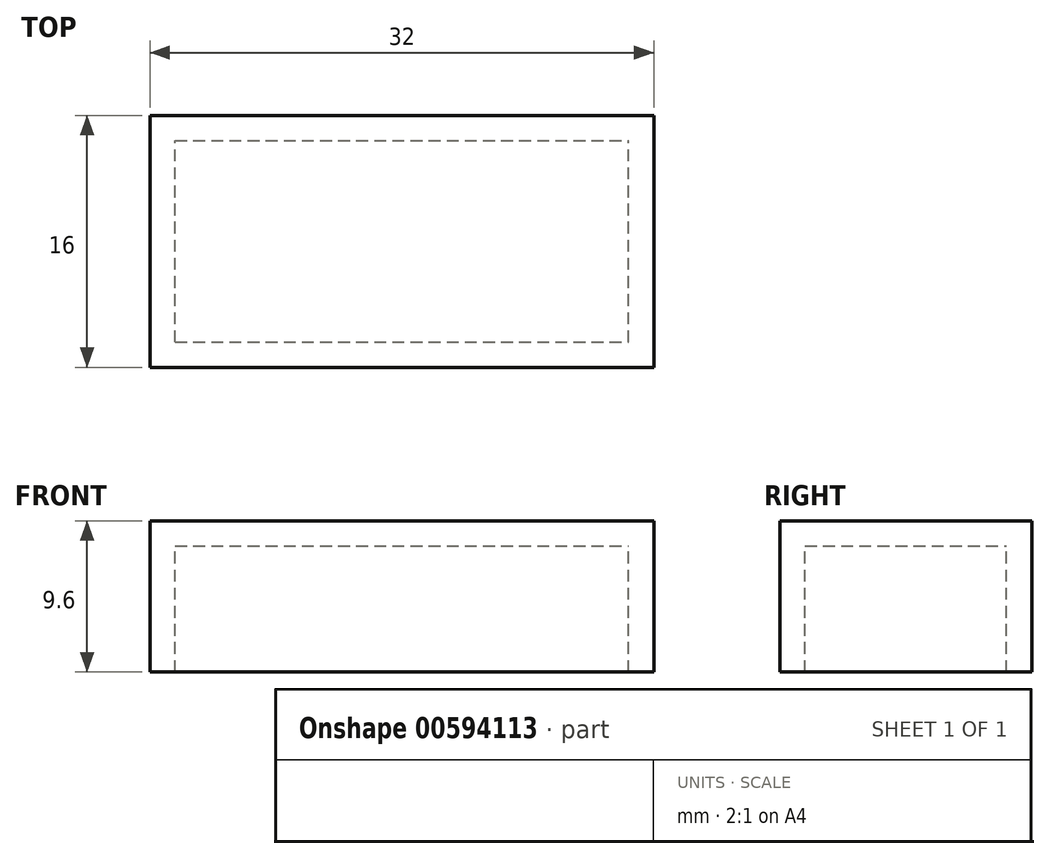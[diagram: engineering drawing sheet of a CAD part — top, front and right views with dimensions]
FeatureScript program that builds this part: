
annotation { "Feature Type Name" : "Feature", "Feature Type Description" : "" }
export const myFeature = defineFeature(function(context is Context, id is Id, definition is map)
    precondition{}
    {
        {
            var Q0;
            Q0=qCreatedBy(makeId("Front.planeOp"),FACE);
            var sketch = newSketch(context, id + "F0", { "sketchPlane" : qUnion([Q0])});
            skLineSegment(sketch, "E0.bottom", {"start": v(-32.95, -27.77) * mm, "end": v(-0.95, -27.77) * mm});
            skLineSegment(sketch, "E0.top", {"start": v(-32.95, -18.17) * mm, "end": v(-0.95, -18.17) * mm});
            skLineSegment(sketch, "E0.left", {"start": v(-32.95, -27.77) * mm, "end": v(-32.95, -18.17) * mm});
            skLineSegment(sketch, "E0.right", {"start": v(-0.95, -27.77) * mm, "end": v(-0.95, -18.17) * mm});
            skSolve(sketch);
        }
        {
            var Q0;
            Q0 = qSketchRegion(id + "F0", true);
            extrude(context, id + "F1", {"entities" : qUnion([Q0]), "depth" : 16 * mm, "offsetDistance" : 25.4 * mm});
        }
        {
            var Q0;
            Q0=makeQuery(id+"F1.opExtrude","SWEPT_FACE",FACE,{"disambiguationData":[OSD([sQuery(id+"F0.wireOp",EDGE,"E0.bottom")])]});
            shell(context, id + "F2", {"entities" : qUnion([Q0]), "thickness" : 1.6 * mm});
        }
    });
